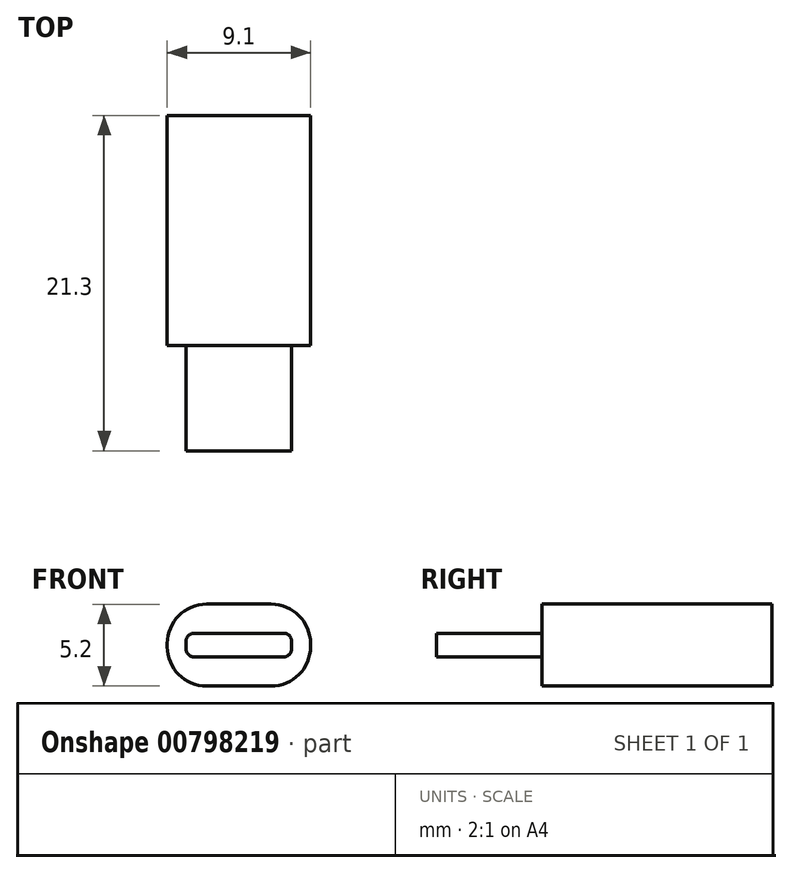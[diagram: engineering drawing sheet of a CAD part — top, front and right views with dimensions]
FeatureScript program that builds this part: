
annotation { "Feature Type Name" : "Feature", "Feature Type Description" : "" }
export const myFeature = defineFeature(function(context is Context, id is Id, definition is map)
    precondition{}
    {
        {
            var Q0;
            Q0=qCreatedBy(makeId("Front.planeOp"),FACE);
            var sketch = newSketch(context, id + "F0", { "sketchPlane" : qUnion([Q0])});
            skLineSegment(sketch, "E0.bottom", {"start": v(2.14, 13.77) * mm, "end": v(11.24, 13.77) * mm});
            skLineSegment(sketch, "E0.top", {"start": v(2.14, 8.57) * mm, "end": v(11.24, 8.57) * mm});
            skLineSegment(sketch, "E0.left", {"start": v(2.14, 13.77) * mm, "end": v(2.14, 8.57) * mm});
            skLineSegment(sketch, "E0.right", {"start": v(11.24, 13.77) * mm, "end": v(11.24, 8.57) * mm});
            skSolve(sketch);
        }
        {
            var Q0;
            Q0=makeQuery(id+"F0.imprint","IMPRINT",FACE,{"disambiguationData":[TD([[makeQuery(id+"F0.imprint","IMPRINT",EDGE,{"derivedFrom":sQuery(id+"F0.wireOp",EDGE,"E0.bottom")}),-1.0]])]});
            extrude(context, id + "F1", {"entities" : qUnion([Q0]), "depth" : 14.6 * mm, "offsetDistance" : 25 * mm});
        }
        {
            var Q0;
            Q0=makeQuery(id+"F1.opExtrude","SWEPT_EDGE",EDGE,{"disambiguationData":[OSD([sQuery(id+"F0.wireOp",EDGE,"E0.top"),sQuery(id+"F0.wireOp",EDGE,"E0.right")])]});
            var Q1;
            Q1=makeQuery(id+"F1.opExtrude","SWEPT_EDGE",EDGE,{"disambiguationData":[OSD([sQuery(id+"F0.wireOp",EDGE,"E0.bottom"),sQuery(id+"F0.wireOp",EDGE,"E0.right")])]});
            var Q2;
            Q2=makeQuery(id+"F1.opExtrude","SWEPT_EDGE",EDGE,{"disambiguationData":[OSD([sQuery(id+"F0.wireOp",EDGE,"E0.top"),sQuery(id+"F0.wireOp",EDGE,"E0.left")])]});
            var Q3;
            Q3=makeQuery(id+"F1.opExtrude","SWEPT_EDGE",EDGE,{"disambiguationData":[OSD([sQuery(id+"F0.wireOp",EDGE,"E0.bottom"),sQuery(id+"F0.wireOp",EDGE,"E0.left")])]});
            fillet(context, id + "F2", {"entities" : qUnion([Q0, Q1, Q2, Q3]), "radius" : 2.5 * mm, "tangentPropagation" : true, "allowEdgeOverflow" : false});
        }
        {
            var Q0;
            Q0=makeQuery(id+"F1.opExtrude","CAP_FACE",FACE,{"disambiguationData":[OSD([sQuery(id+"F0.wireOp",EDGE,"E0.bottom"),sQuery(id+"F0.wireOp",EDGE,"E0.top"),sQuery(id+"F0.wireOp",EDGE,"E0.left"),sQuery(id+"F0.wireOp",EDGE,"E0.right")])],"isStart":false});
            var sketch = newSketch(context, id + "F3", { "sketchPlane" : qUnion([Q0])});
            skPoint(sketch, "E1.0", {"position": v(6.7, 13.77) * mm});
            skPoint(sketch, "E2.0", {"position": v(6.7, 8.57) * mm});
            skLineSegment(sketch, "E3", {"start": v(6.7, 13.77) * mm, "end": v(6.7, 8.57) * mm, "construction": true});
            skLineSegment(sketch, "E4.bottom", {"start": v(10.04, 11.92) * mm, "end": v(3.34, 11.92) * mm});
            skLineSegment(sketch, "E4.top", {"start": v(10.04, 10.42) * mm, "end": v(3.34, 10.42) * mm});
            skLineSegment(sketch, "E4.left", {"start": v(10.04, 11.92) * mm, "end": v(10.04, 10.42) * mm});
            skLineSegment(sketch, "E4.right", {"start": v(3.34, 11.92) * mm, "end": v(3.34, 10.42) * mm});
            skPoint(sketch, "E4.middle", {"position": v(6.7, 11.17) * mm});
            skSolve(sketch);
        }
        {
            var Q0;
            Q0=makeQuery(id+"F3.imprint","IMPRINT",FACE,{"disambiguationData":[TD([[makeQuery(id+"F3.imprint","IMPRINT",EDGE,{"derivedFrom":sQuery(id+"F3.wireOp",EDGE,"E4.bottom")}),1.0]])]});
            extrude(context, id + "F4", {"entities" : qUnion([Q0]), "operationType" : NewBodyOperationType.ADD, "depth" : 6.7 * mm, "offsetDistance" : 25 * mm});
        }
        {
            var Q0;
            Q0=makeQuery(id+"F4.opExtrude","SWEPT_EDGE",EDGE,{"disambiguationData":[OSD([sQuery(id+"F3.wireOp",EDGE,"E4.top"),sQuery(id+"F3.wireOp",EDGE,"E4.right")])]});
            var Q1;
            Q1=makeQuery(id+"F4.opExtrude","SWEPT_EDGE",EDGE,{"disambiguationData":[OSD([sQuery(id+"F3.wireOp",EDGE,"E4.top"),sQuery(id+"F3.wireOp",EDGE,"E4.left")])]});
            var Q2;
            Q2=makeQuery(id+"F4.opExtrude","SWEPT_EDGE",EDGE,{"disambiguationData":[OSD([sQuery(id+"F3.wireOp",EDGE,"E4.bottom"),sQuery(id+"F3.wireOp",EDGE,"E4.left")])]});
            var Q3;
            Q3=makeQuery(id+"F4.opExtrude","SWEPT_EDGE",EDGE,{"disambiguationData":[OSD([sQuery(id+"F3.wireOp",EDGE,"E4.bottom"),sQuery(id+"F3.wireOp",EDGE,"E4.right")])]});
            fillet(context, id + "F5", {"entities" : qUnion([Q0, Q1, Q2, Q3]), "radius" : 0.5 * mm, "tangentPropagation" : true, "allowEdgeOverflow" : false});
        }
    });
